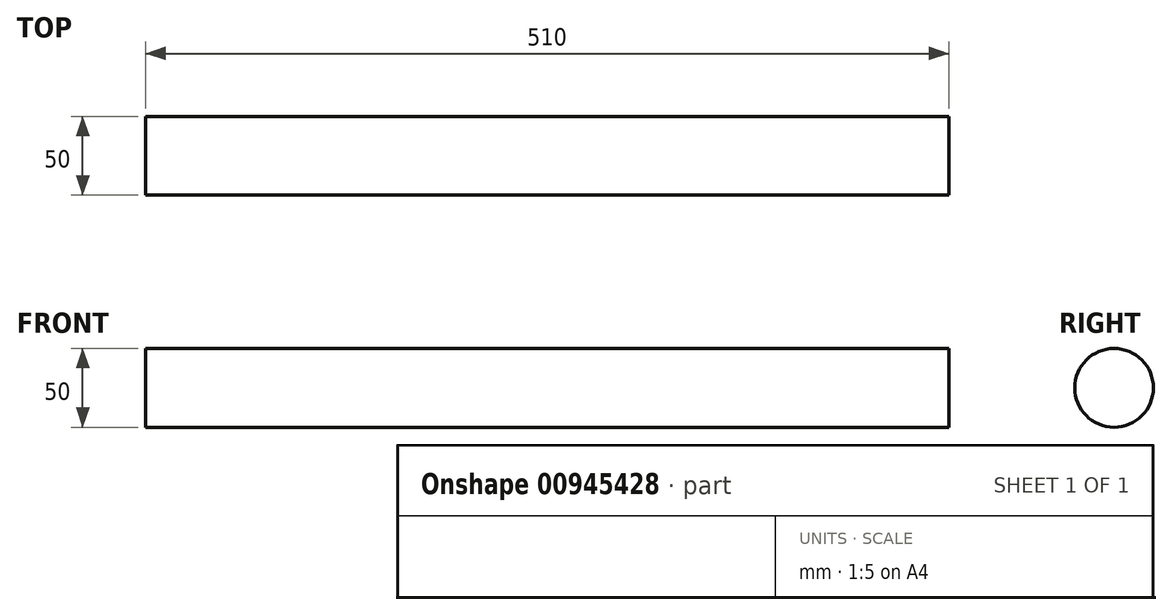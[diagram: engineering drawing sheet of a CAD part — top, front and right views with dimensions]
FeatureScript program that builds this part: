
annotation { "Feature Type Name" : "Feature", "Feature Type Description" : "" }
export const myFeature = defineFeature(function(context is Context, id is Id, definition is map)
    precondition{}
    {
        {
            var Q0;
            Q0=qCreatedBy(makeId("Right.planeOp"),FACE);
            var sketch = newSketch(context, id + "F0", { "sketchPlane" : qUnion([Q0])});
            skCircle(sketch, "E0", {"center": v(0, 0) * mm, "radius": 25 * mm});
            skSolve(sketch);
        }
        {
            var Q0;
            Q0=sQuery(id+"F0.wireOp",EDGE,"E0");
            extrude(context, id + "F1", {"bodyType" : ToolBodyType.SURFACE, "surfaceEntities" : qUnion([Q0]), "depth" : 510 * mm, "offsetDistance" : 25.4 * mm});
        }
    });
